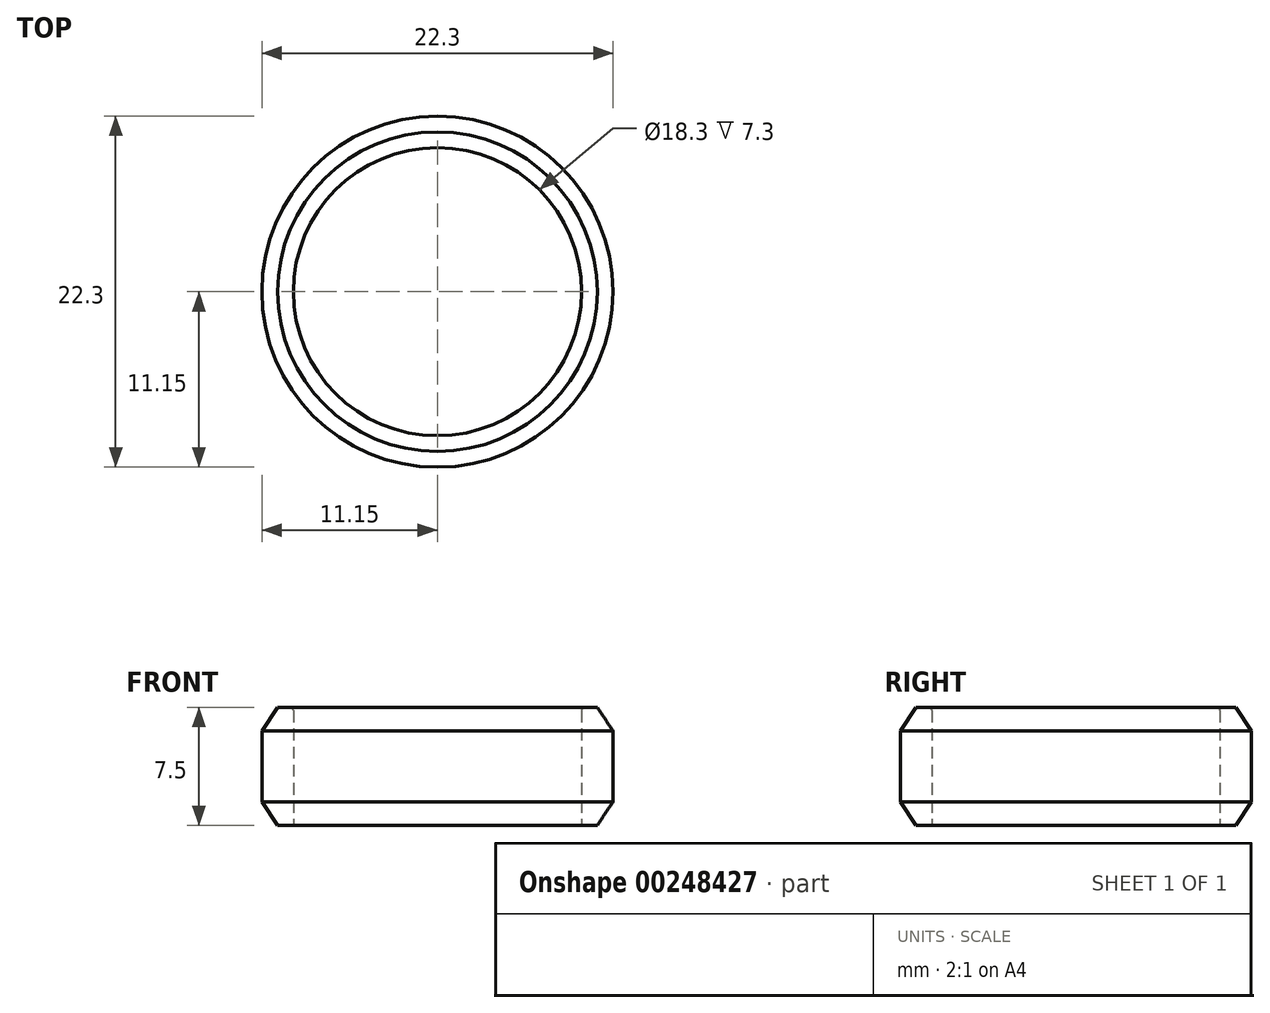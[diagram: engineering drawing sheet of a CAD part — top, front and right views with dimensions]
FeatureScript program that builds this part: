
annotation { "Feature Type Name" : "Feature", "Feature Type Description" : "" }
export const myFeature = defineFeature(function(context is Context, id is Id, definition is map)
    precondition{}
    {
        {
            var Q0;
            Q0=qCreatedBy(makeId("Top.planeOp"),FACE);
            var sketch = newSketch(context, id + "F0", { "sketchPlane" : qUnion([Q0])});
            skCircle(sketch, "E0", {"center": v(0, 0) * mm, "radius": 9.15 * mm});
            skCircle(sketch, "E1.0", {"center": v(0, 0) * mm, "radius": 11.15 * mm});
            skPoint(sketch, "E2", {"position": v(0, 10.15) * mm});
            skPoint(sketch, "E3.start.orphan", {"position": v(0, 11.15) * mm});
            skPoint(sketch, "E4.trimOffspring.end.orphan", {"position": v(0, 9.15) * mm});
            skSolve(sketch);
        }
        {
            var Q0;
            Q0=makeQuery(id+"F0.imprint","IMPRINT",FACE,{"disambiguationData":[TD([[makeQuery(id+"F0.imprint","IMPRINT",EDGE,{"derivedFrom":sQuery(id+"F0.wireOp",EDGE,"E0")}),-1.0]])]});
            var Q1;
            Q1=makeQuery(id+"F0.imprint","IMPRINT",FACE,{"disambiguationData":[TD([[makeQuery(id+"F0.imprint","IMPRINT",EDGE,{"derivedFrom":sQuery(id+"F0.wireOp",EDGE,"a28f23ed-ef4f-4aed-836b-e849da1a0182.1.61.0")}),1.0]])]});
            var Q2;
            Q2=makeQuery(id+"F0.imprint","IMPRINT",FACE,{"disambiguationData":[TD([[makeQuery(id+"F0.imprint","IMPRINT",EDGE,{"derivedFrom":sQuery(id+"F0.wireOp",EDGE,"9b5bb41e-afbc-4d25-b2b3-00661ebed94f.1.26.0")}),1.0]])]});
            var Q3;
            Q3=makeQuery(id+"F0.imprint","IMPRINT",FACE,{"disambiguationData":[TD([[makeQuery(id+"F0.imprint","IMPRINT",EDGE,{"derivedFrom":sQuery(id+"F0.wireOp",EDGE,"6a247efb-4b51-4912-8876-f2ab3c554f81.10.0")}),1.0]])]});
            var Q4;
            Q4=makeQuery(id+"F0.imprint","IMPRINT",FACE,{"disambiguationData":[TD([[makeQuery(id+"F0.imprint","IMPRINT",EDGE,{"derivedFrom":sQuery(id+"F0.wireOp",EDGE,"a28f23ed-ef4f-4aed-836b-e849da1a0182.1.75.0")}),1.0]])]});
            var Q5;
            Q5=makeQuery(id+"F0.imprint","IMPRINT",FACE,{"disambiguationData":[TD([[makeQuery(id+"F0.imprint","IMPRINT",EDGE,{"derivedFrom":sQuery(id+"F0.wireOp",EDGE,"0dfb17a8-0a4b-4796-96ea-2a2d021c0c5c.1.42.0")}),1.0]])]});
            var Q6;
            Q6=makeQuery(id+"F0.imprint","IMPRINT",FACE,{"disambiguationData":[TD([[makeQuery(id+"F0.imprint","IMPRINT",EDGE,{"derivedFrom":sQuery(id+"F0.wireOp",EDGE,"0dfb17a8-0a4b-4796-96ea-2a2d021c0c5c.1.37.0")}),1.0]])]});
            var Q7;
            Q7=makeQuery(id+"F0.imprint","IMPRINT",FACE,{"disambiguationData":[TD([[makeQuery(id+"F0.imprint","IMPRINT",EDGE,{"derivedFrom":sQuery(id+"F0.wireOp",EDGE,"6a247efb-4b51-4912-8876-f2ab3c554f81.13.0")}),1.0]])]});
            var Q8;
            Q8=makeQuery(id+"F0.imprint","IMPRINT",FACE,{"disambiguationData":[TD([[makeQuery(id+"F0.imprint","IMPRINT",EDGE,{"derivedFrom":sQuery(id+"F0.wireOp",EDGE,"a28f23ed-ef4f-4aed-836b-e849da1a0182.1.68.0")}),1.0]])]});
            var Q9;
            Q9=makeQuery(id+"F0.imprint","IMPRINT",FACE,{"disambiguationData":[TD([[makeQuery(id+"F0.imprint","IMPRINT",EDGE,{"derivedFrom":sQuery(id+"F0.wireOp",EDGE,"a28f23ed-ef4f-4aed-836b-e849da1a0182.1.71.0")}),1.0]])]});
            var Q10;
            Q10=makeQuery(id+"F0.imprint","IMPRINT",FACE,{"disambiguationData":[TD([[makeQuery(id+"F0.imprint","IMPRINT",EDGE,{"derivedFrom":sQuery(id+"F0.wireOp",EDGE,"9b5bb41e-afbc-4d25-b2b3-00661ebed94f.1.28.0")}),1.0]])]});
            var Q11;
            Q11=makeQuery(id+"F0.imprint","IMPRINT",FACE,{"disambiguationData":[TD([[makeQuery(id+"F0.imprint","IMPRINT",EDGE,{"derivedFrom":sQuery(id+"F0.wireOp",EDGE,"9b5bb41e-afbc-4d25-b2b3-00661ebed94f.1.29.0")}),1.0]])]});
            var Q12;
            Q12=makeQuery(id+"F0.imprint","IMPRINT",FACE,{"disambiguationData":[TD([[makeQuery(id+"F0.imprint","IMPRINT",EDGE,{"derivedFrom":sQuery(id+"F0.wireOp",EDGE,"0dfb17a8-0a4b-4796-96ea-2a2d021c0c5c.1.51.0")}),1.0]])]});
            var Q13;
            Q13=makeQuery(id+"F0.imprint","IMPRINT",FACE,{"disambiguationData":[TD([[makeQuery(id+"F0.imprint","IMPRINT",EDGE,{"derivedFrom":sQuery(id+"F0.wireOp",EDGE,"6a247efb-4b51-4912-8876-f2ab3c554f81.9.0")}),1.0]])]});
            var Q14;
            Q14=makeQuery(id+"F0.imprint","IMPRINT",FACE,{"disambiguationData":[TD([[makeQuery(id+"F0.imprint","IMPRINT",EDGE,{"derivedFrom":sQuery(id+"F0.wireOp",EDGE,"dd421f76-6e49-4080-92ba-426d591658a1")}),1.0]])]});
            var Q15;
            Q15=makeQuery(id+"F0.imprint","IMPRINT",FACE,{"disambiguationData":[TD([[makeQuery(id+"F0.imprint","IMPRINT",EDGE,{"derivedFrom":sQuery(id+"F0.wireOp",EDGE,"0dfb17a8-0a4b-4796-96ea-2a2d021c0c5c.1.57.0")}),1.0]])]});
            var Q16;
            Q16=makeQuery(id+"F0.imprint","IMPRINT",FACE,{"disambiguationData":[TD([[makeQuery(id+"F0.imprint","IMPRINT",EDGE,{"derivedFrom":sQuery(id+"F0.wireOp",EDGE,"a28f23ed-ef4f-4aed-836b-e849da1a0182.1.63.0")}),1.0]])]});
            var Q17;
            Q17=makeQuery(id+"F0.imprint","IMPRINT",FACE,{"disambiguationData":[TD([[makeQuery(id+"F0.imprint","IMPRINT",EDGE,{"derivedFrom":sQuery(id+"F0.wireOp",EDGE,"6a247efb-4b51-4912-8876-f2ab3c554f81.6.0")}),1.0]])]});
            var Q18;
            Q18=makeQuery(id+"F0.imprint","IMPRINT",FACE,{"disambiguationData":[TD([[makeQuery(id+"F0.imprint","IMPRINT",EDGE,{"derivedFrom":sQuery(id+"F0.wireOp",EDGE,"6a247efb-4b51-4912-8876-f2ab3c554f81.17.0")}),1.0]])]});
            var Q19;
            Q19=makeQuery(id+"F0.imprint","IMPRINT",FACE,{"disambiguationData":[TD([[makeQuery(id+"F0.imprint","IMPRINT",EDGE,{"derivedFrom":sQuery(id+"F0.wireOp",EDGE,"a28f23ed-ef4f-4aed-836b-e849da1a0182.1.74.0")}),1.0]])]});
            var Q20;
            Q20=makeQuery(id+"F0.imprint","IMPRINT",FACE,{"disambiguationData":[TD([[makeQuery(id+"F0.imprint","IMPRINT",EDGE,{"derivedFrom":sQuery(id+"F0.wireOp",EDGE,"9b5bb41e-afbc-4d25-b2b3-00661ebed94f.1.25.0")}),1.0]])]});
            var Q21;
            Q21=makeQuery(id+"F0.imprint","IMPRINT",FACE,{"disambiguationData":[TD([[makeQuery(id+"F0.imprint","IMPRINT",EDGE,{"derivedFrom":sQuery(id+"F0.wireOp",EDGE,"6a247efb-4b51-4912-8876-f2ab3c554f81.22.0")}),1.0]])]});
            var Q22;
            Q22=makeQuery(id+"F0.imprint","IMPRINT",FACE,{"disambiguationData":[TD([[makeQuery(id+"F0.imprint","IMPRINT",EDGE,{"derivedFrom":sQuery(id+"F0.wireOp",EDGE,"6a247efb-4b51-4912-8876-f2ab3c554f81.14.0")}),1.0]])]});
            var Q23;
            Q23=makeQuery(id+"F0.imprint","IMPRINT",FACE,{"disambiguationData":[TD([[makeQuery(id+"F0.imprint","IMPRINT",EDGE,{"derivedFrom":sQuery(id+"F0.wireOp",EDGE,"a28f23ed-ef4f-4aed-836b-e849da1a0182.1.77.0")}),1.0]])]});
            var Q24;
            Q24=makeQuery(id+"F0.imprint","IMPRINT",FACE,{"disambiguationData":[TD([[makeQuery(id+"F0.imprint","IMPRINT",EDGE,{"derivedFrom":sQuery(id+"F0.wireOp",EDGE,"6a247efb-4b51-4912-8876-f2ab3c554f81.16.0")}),1.0]])]});
            var Q25;
            Q25=makeQuery(id+"F0.imprint","IMPRINT",FACE,{"disambiguationData":[TD([[makeQuery(id+"F0.imprint","IMPRINT",EDGE,{"derivedFrom":sQuery(id+"F0.wireOp",EDGE,"a28f23ed-ef4f-4aed-836b-e849da1a0182.1.64.0")}),1.0]])]});
            var Q26;
            Q26=makeQuery(id+"F0.imprint","IMPRINT",FACE,{"disambiguationData":[TD([[makeQuery(id+"F0.imprint","IMPRINT",EDGE,{"derivedFrom":sQuery(id+"F0.wireOp",EDGE,"9b5bb41e-afbc-4d25-b2b3-00661ebed94f.1.31.0")}),1.0]])]});
            var Q27;
            Q27=makeQuery(id+"F0.imprint","IMPRINT",FACE,{"disambiguationData":[TD([[makeQuery(id+"F0.imprint","IMPRINT",EDGE,{"derivedFrom":sQuery(id+"F0.wireOp",EDGE,"6a247efb-4b51-4912-8876-f2ab3c554f81.2.0")}),1.0]])]});
            var Q28;
            Q28=makeQuery(id+"F0.imprint","IMPRINT",FACE,{"disambiguationData":[TD([[makeQuery(id+"F0.imprint","IMPRINT",EDGE,{"derivedFrom":sQuery(id+"F0.wireOp",EDGE,"6a247efb-4b51-4912-8876-f2ab3c554f81.20.0")}),1.0]])]});
            var Q29;
            Q29=makeQuery(id+"F0.imprint","IMPRINT",FACE,{"disambiguationData":[TD([[makeQuery(id+"F0.imprint","IMPRINT",EDGE,{"derivedFrom":sQuery(id+"F0.wireOp",EDGE,"a28f23ed-ef4f-4aed-836b-e849da1a0182.1.69.0")}),1.0]])]});
            var Q30;
            Q30=makeQuery(id+"F0.imprint","IMPRINT",FACE,{"disambiguationData":[TD([[makeQuery(id+"F0.imprint","IMPRINT",EDGE,{"derivedFrom":sQuery(id+"F0.wireOp",EDGE,"0dfb17a8-0a4b-4796-96ea-2a2d021c0c5c.1.59.0")}),1.0]])]});
            var Q31;
            Q31=makeQuery(id+"F0.imprint","IMPRINT",FACE,{"disambiguationData":[TD([[makeQuery(id+"F0.imprint","IMPRINT",EDGE,{"derivedFrom":sQuery(id+"F0.wireOp",EDGE,"6a247efb-4b51-4912-8876-f2ab3c554f81.15.0")}),1.0]])]});
            var Q32;
            Q32=makeQuery(id+"F0.imprint","IMPRINT",FACE,{"disambiguationData":[TD([[makeQuery(id+"F0.imprint","IMPRINT",EDGE,{"derivedFrom":sQuery(id+"F0.wireOp",EDGE,"6a247efb-4b51-4912-8876-f2ab3c554f81.4.0")}),1.0]])]});
            var Q33;
            Q33=makeQuery(id+"F0.imprint","IMPRINT",FACE,{"disambiguationData":[TD([[makeQuery(id+"F0.imprint","IMPRINT",EDGE,{"derivedFrom":sQuery(id+"F0.wireOp",EDGE,"0dfb17a8-0a4b-4796-96ea-2a2d021c0c5c.1.55.0")}),1.0]])]});
            var Q34;
            Q34=makeQuery(id+"F0.imprint","IMPRINT",FACE,{"disambiguationData":[TD([[makeQuery(id+"F0.imprint","IMPRINT",EDGE,{"derivedFrom":sQuery(id+"F0.wireOp",EDGE,"a28f23ed-ef4f-4aed-836b-e849da1a0182.1.62.0")}),1.0]])]});
            var Q35;
            Q35=makeQuery(id+"F0.imprint","IMPRINT",FACE,{"disambiguationData":[TD([[makeQuery(id+"F0.imprint","IMPRINT",EDGE,{"derivedFrom":sQuery(id+"F0.wireOp",EDGE,"0dfb17a8-0a4b-4796-96ea-2a2d021c0c5c.1.39.0")}),1.0]])]});
            var Q36;
            Q36=makeQuery(id+"F0.imprint","IMPRINT",FACE,{"disambiguationData":[TD([[makeQuery(id+"F0.imprint","IMPRINT",EDGE,{"derivedFrom":sQuery(id+"F0.wireOp",EDGE,"6a247efb-4b51-4912-8876-f2ab3c554f81.7.0")}),1.0]])]});
            var Q37;
            Q37=makeQuery(id+"F0.imprint","IMPRINT",FACE,{"disambiguationData":[TD([[makeQuery(id+"F0.imprint","IMPRINT",EDGE,{"derivedFrom":sQuery(id+"F0.wireOp",EDGE,"0dfb17a8-0a4b-4796-96ea-2a2d021c0c5c.1.45.0")}),1.0]])]});
            var Q38;
            Q38=makeQuery(id+"F0.imprint","IMPRINT",FACE,{"disambiguationData":[TD([[makeQuery(id+"F0.imprint","IMPRINT",EDGE,{"derivedFrom":sQuery(id+"F0.wireOp",EDGE,"6a247efb-4b51-4912-8876-f2ab3c554f81.11.0")}),1.0]])]});
            var Q39;
            Q39=makeQuery(id+"F0.imprint","IMPRINT",FACE,{"disambiguationData":[TD([[makeQuery(id+"F0.imprint","IMPRINT",EDGE,{"derivedFrom":sQuery(id+"F0.wireOp",EDGE,"0dfb17a8-0a4b-4796-96ea-2a2d021c0c5c.1.43.0")}),1.0]])]});
            var Q40;
            Q40=makeQuery(id+"F0.imprint","IMPRINT",FACE,{"disambiguationData":[TD([[makeQuery(id+"F0.imprint","IMPRINT",EDGE,{"derivedFrom":sQuery(id+"F0.wireOp",EDGE,"0dfb17a8-0a4b-4796-96ea-2a2d021c0c5c.1.54.0")}),1.0]])]});
            var Q41;
            Q41=makeQuery(id+"F0.imprint","IMPRINT",FACE,{"disambiguationData":[TD([[makeQuery(id+"F0.imprint","IMPRINT",EDGE,{"derivedFrom":sQuery(id+"F0.wireOp",EDGE,"6a247efb-4b51-4912-8876-f2ab3c554f81.1.0")}),1.0]])]});
            var Q42;
            Q42=makeQuery(id+"F0.imprint","IMPRINT",FACE,{"disambiguationData":[TD([[makeQuery(id+"F0.imprint","IMPRINT",EDGE,{"derivedFrom":sQuery(id+"F0.wireOp",EDGE,"a28f23ed-ef4f-4aed-836b-e849da1a0182.1.70.0")}),1.0]])]});
            var Q43;
            Q43=makeQuery(id+"F0.imprint","IMPRINT",FACE,{"disambiguationData":[TD([[makeQuery(id+"F0.imprint","IMPRINT",EDGE,{"derivedFrom":sQuery(id+"F0.wireOp",EDGE,"0dfb17a8-0a4b-4796-96ea-2a2d021c0c5c.1.38.0")}),1.0]])]});
            var Q44;
            Q44=makeQuery(id+"F0.imprint","IMPRINT",FACE,{"disambiguationData":[TD([[makeQuery(id+"F0.imprint","IMPRINT",EDGE,{"derivedFrom":sQuery(id+"F0.wireOp",EDGE,"0dfb17a8-0a4b-4796-96ea-2a2d021c0c5c.1.48.0")}),1.0]])]});
            var Q45;
            Q45=makeQuery(id+"F0.imprint","IMPRINT",FACE,{"disambiguationData":[TD([[makeQuery(id+"F0.imprint","IMPRINT",EDGE,{"derivedFrom":sQuery(id+"F0.wireOp",EDGE,"a28f23ed-ef4f-4aed-836b-e849da1a0182.1.76.0")}),1.0]])]});
            var Q46;
            Q46=makeQuery(id+"F0.imprint","IMPRINT",FACE,{"disambiguationData":[TD([[makeQuery(id+"F0.imprint","IMPRINT",EDGE,{"derivedFrom":sQuery(id+"F0.wireOp",EDGE,"0dfb17a8-0a4b-4796-96ea-2a2d021c0c5c.1.50.0")}),1.0]])]});
            var Q47;
            Q47=makeQuery(id+"F0.imprint","IMPRINT",FACE,{"disambiguationData":[TD([[makeQuery(id+"F0.imprint","IMPRINT",EDGE,{"derivedFrom":sQuery(id+"F0.wireOp",EDGE,"6a247efb-4b51-4912-8876-f2ab3c554f81.18.0")}),1.0]])]});
            var Q48;
            Q48=makeQuery(id+"F0.imprint","IMPRINT",FACE,{"disambiguationData":[TD([[makeQuery(id+"F0.imprint","IMPRINT",EDGE,{"derivedFrom":sQuery(id+"F0.wireOp",EDGE,"9b5bb41e-afbc-4d25-b2b3-00661ebed94f.1.33.0")}),1.0]])]});
            var Q49;
            Q49=makeQuery(id+"F0.imprint","IMPRINT",FACE,{"disambiguationData":[TD([[makeQuery(id+"F0.imprint","IMPRINT",EDGE,{"derivedFrom":sQuery(id+"F0.wireOp",EDGE,"a28f23ed-ef4f-4aed-836b-e849da1a0182.1.65.0")}),1.0]])]});
            var Q50;
            Q50=makeQuery(id+"F0.imprint","IMPRINT",FACE,{"disambiguationData":[TD([[makeQuery(id+"F0.imprint","IMPRINT",EDGE,{"derivedFrom":sQuery(id+"F0.wireOp",EDGE,"0dfb17a8-0a4b-4796-96ea-2a2d021c0c5c.1.49.0")}),1.0]])]});
            var Q51;
            Q51=makeQuery(id+"F0.imprint","IMPRINT",FACE,{"disambiguationData":[TD([[makeQuery(id+"F0.imprint","IMPRINT",EDGE,{"derivedFrom":sQuery(id+"F0.wireOp",EDGE,"6a247efb-4b51-4912-8876-f2ab3c554f81.23.0")}),1.0]])]});
            var Q52;
            Q52=makeQuery(id+"F0.imprint","IMPRINT",FACE,{"disambiguationData":[TD([[makeQuery(id+"F0.imprint","IMPRINT",EDGE,{"derivedFrom":sQuery(id+"F0.wireOp",EDGE,"0dfb17a8-0a4b-4796-96ea-2a2d021c0c5c.1.58.0")}),1.0]])]});
            var Q53;
            Q53=makeQuery(id+"F0.imprint","IMPRINT",FACE,{"disambiguationData":[TD([[makeQuery(id+"F0.imprint","IMPRINT",EDGE,{"derivedFrom":sQuery(id+"F0.wireOp",EDGE,"6a247efb-4b51-4912-8876-f2ab3c554f81.12.0")}),1.0]])]});
            var Q54;
            Q54=makeQuery(id+"F0.imprint","IMPRINT",FACE,{"disambiguationData":[TD([[makeQuery(id+"F0.imprint","IMPRINT",EDGE,{"derivedFrom":sQuery(id+"F0.wireOp",EDGE,"9b5bb41e-afbc-4d25-b2b3-00661ebed94f.1.32.0")}),1.0]])]});
            var Q55;
            Q55=makeQuery(id+"F0.imprint","IMPRINT",FACE,{"disambiguationData":[TD([[makeQuery(id+"F0.imprint","IMPRINT",EDGE,{"derivedFrom":sQuery(id+"F0.wireOp",EDGE,"0dfb17a8-0a4b-4796-96ea-2a2d021c0c5c.1.41.0")}),1.0]])]});
            var Q56;
            Q56=makeQuery(id+"F0.imprint","IMPRINT",FACE,{"disambiguationData":[TD([[makeQuery(id+"F0.imprint","IMPRINT",EDGE,{"derivedFrom":sQuery(id+"F0.wireOp",EDGE,"9b5bb41e-afbc-4d25-b2b3-00661ebed94f.1.34.0")}),1.0]])]});
            var Q57;
            Q57=makeQuery(id+"F0.imprint","IMPRINT",FACE,{"disambiguationData":[TD([[makeQuery(id+"F0.imprint","IMPRINT",EDGE,{"derivedFrom":sQuery(id+"F0.wireOp",EDGE,"a28f23ed-ef4f-4aed-836b-e849da1a0182.1.67.0")}),1.0]])]});
            var Q58;
            Q58=makeQuery(id+"F0.imprint","IMPRINT",FACE,{"disambiguationData":[TD([[makeQuery(id+"F0.imprint","IMPRINT",EDGE,{"derivedFrom":sQuery(id+"F0.wireOp",EDGE,"0dfb17a8-0a4b-4796-96ea-2a2d021c0c5c.1.46.0")}),1.0]])]});
            var Q59;
            Q59=makeQuery(id+"F0.imprint","IMPRINT",FACE,{"disambiguationData":[TD([[makeQuery(id+"F0.imprint","IMPRINT",EDGE,{"derivedFrom":sQuery(id+"F0.wireOp",EDGE,"0dfb17a8-0a4b-4796-96ea-2a2d021c0c5c.1.36.0")}),1.0]])]});
            var Q60;
            Q60=makeQuery(id+"F0.imprint","IMPRINT",FACE,{"disambiguationData":[TD([[makeQuery(id+"F0.imprint","IMPRINT",EDGE,{"derivedFrom":sQuery(id+"F0.wireOp",EDGE,"a28f23ed-ef4f-4aed-836b-e849da1a0182.1.60.0")}),1.0]])]});
            var Q61;
            Q61=makeQuery(id+"F0.imprint","IMPRINT",FACE,{"disambiguationData":[TD([[makeQuery(id+"F0.imprint","IMPRINT",EDGE,{"derivedFrom":sQuery(id+"F0.wireOp",EDGE,"a28f23ed-ef4f-4aed-836b-e849da1a0182.1.66.0")}),1.0]])]});
            var Q62;
            Q62=makeQuery(id+"F0.imprint","IMPRINT",FACE,{"disambiguationData":[TD([[makeQuery(id+"F0.imprint","IMPRINT",EDGE,{"derivedFrom":sQuery(id+"F0.wireOp",EDGE,"0dfb17a8-0a4b-4796-96ea-2a2d021c0c5c.1.56.0")}),1.0]])]});
            var Q63;
            Q63=makeQuery(id+"F0.imprint","IMPRINT",FACE,{"disambiguationData":[TD([[makeQuery(id+"F0.imprint","IMPRINT",EDGE,{"derivedFrom":sQuery(id+"F0.wireOp",EDGE,"9b5bb41e-afbc-4d25-b2b3-00661ebed94f.1.30.0")}),1.0]])]});
            var Q64;
            Q64=makeQuery(id+"F0.imprint","IMPRINT",FACE,{"disambiguationData":[TD([[makeQuery(id+"F0.imprint","IMPRINT",EDGE,{"derivedFrom":sQuery(id+"F0.wireOp",EDGE,"6a247efb-4b51-4912-8876-f2ab3c554f81.8.0")}),1.0]])]});
            var Q65;
            Q65=makeQuery(id+"F0.imprint","IMPRINT",FACE,{"disambiguationData":[TD([[makeQuery(id+"F0.imprint","IMPRINT",EDGE,{"derivedFrom":sQuery(id+"F0.wireOp",EDGE,"0dfb17a8-0a4b-4796-96ea-2a2d021c0c5c.1.52.0")}),1.0]])]});
            var Q66;
            Q66=makeQuery(id+"F0.imprint","IMPRINT",FACE,{"disambiguationData":[TD([[makeQuery(id+"F0.imprint","IMPRINT",EDGE,{"derivedFrom":sQuery(id+"F0.wireOp",EDGE,"0dfb17a8-0a4b-4796-96ea-2a2d021c0c5c.1.53.0")}),1.0]])]});
            var Q67;
            Q67=makeQuery(id+"F0.imprint","IMPRINT",FACE,{"disambiguationData":[TD([[makeQuery(id+"F0.imprint","IMPRINT",EDGE,{"derivedFrom":sQuery(id+"F0.wireOp",EDGE,"6a247efb-4b51-4912-8876-f2ab3c554f81.5.0")}),1.0]])]});
            var Q68;
            Q68=makeQuery(id+"F0.imprint","IMPRINT",FACE,{"disambiguationData":[TD([[makeQuery(id+"F0.imprint","IMPRINT",EDGE,{"derivedFrom":sQuery(id+"F0.wireOp",EDGE,"a28f23ed-ef4f-4aed-836b-e849da1a0182.1.72.0")}),1.0]])]});
            var Q69;
            Q69=makeQuery(id+"F0.imprint","IMPRINT",FACE,{"disambiguationData":[TD([[makeQuery(id+"F0.imprint","IMPRINT",EDGE,{"derivedFrom":sQuery(id+"F0.wireOp",EDGE,"0dfb17a8-0a4b-4796-96ea-2a2d021c0c5c.1.40.0")}),1.0]])]});
            var Q70;
            Q70=makeQuery(id+"F0.imprint","IMPRINT",FACE,{"disambiguationData":[TD([[makeQuery(id+"F0.imprint","IMPRINT",EDGE,{"derivedFrom":sQuery(id+"F0.wireOp",EDGE,"0dfb17a8-0a4b-4796-96ea-2a2d021c0c5c.1.47.0")}),1.0]])]});
            var Q71;
            Q71=makeQuery(id+"F0.imprint","IMPRINT",FACE,{"disambiguationData":[TD([[makeQuery(id+"F0.imprint","IMPRINT",EDGE,{"derivedFrom":sQuery(id+"F0.wireOp",EDGE,"6a247efb-4b51-4912-8876-f2ab3c554f81.3.0")}),1.0]])]});
            var Q72;
            Q72=makeQuery(id+"F0.imprint","IMPRINT",FACE,{"disambiguationData":[TD([[makeQuery(id+"F0.imprint","IMPRINT",EDGE,{"derivedFrom":sQuery(id+"F0.wireOp",EDGE,"a28f23ed-ef4f-4aed-836b-e849da1a0182.1.79.0")}),1.0]])]});
            var Q73;
            Q73=makeQuery(id+"F0.imprint","IMPRINT",FACE,{"disambiguationData":[TD([[makeQuery(id+"F0.imprint","IMPRINT",EDGE,{"derivedFrom":sQuery(id+"F0.wireOp",EDGE,"6a247efb-4b51-4912-8876-f2ab3c554f81.24.0")}),1.0]])]});
            var Q74;
            Q74=makeQuery(id+"F0.imprint","IMPRINT",FACE,{"disambiguationData":[TD([[makeQuery(id+"F0.imprint","IMPRINT",EDGE,{"derivedFrom":sQuery(id+"F0.wireOp",EDGE,"a28f23ed-ef4f-4aed-836b-e849da1a0182.1.78.0")}),1.0]])]});
            var Q75;
            Q75=makeQuery(id+"F0.imprint","IMPRINT",FACE,{"disambiguationData":[TD([[makeQuery(id+"F0.imprint","IMPRINT",EDGE,{"derivedFrom":sQuery(id+"F0.wireOp",EDGE,"6a247efb-4b51-4912-8876-f2ab3c554f81.21.0")}),1.0]])]});
            var Q76;
            Q76=makeQuery(id+"F0.imprint","IMPRINT",FACE,{"disambiguationData":[TD([[makeQuery(id+"F0.imprint","IMPRINT",EDGE,{"derivedFrom":sQuery(id+"F0.wireOp",EDGE,"0dfb17a8-0a4b-4796-96ea-2a2d021c0c5c.1.44.0")}),1.0]])]});
            var Q77;
            Q77=makeQuery(id+"F0.imprint","IMPRINT",FACE,{"disambiguationData":[TD([[makeQuery(id+"F0.imprint","IMPRINT",EDGE,{"derivedFrom":sQuery(id+"F0.wireOp",EDGE,"9b5bb41e-afbc-4d25-b2b3-00661ebed94f.1.27.0")}),1.0]])]});
            var Q78;
            Q78=makeQuery(id+"F0.imprint","IMPRINT",FACE,{"disambiguationData":[TD([[makeQuery(id+"F0.imprint","IMPRINT",EDGE,{"derivedFrom":sQuery(id+"F0.wireOp",EDGE,"a28f23ed-ef4f-4aed-836b-e849da1a0182.1.73.0")}),1.0]])]});
            var Q79;
            Q79=makeQuery(id+"F0.imprint","IMPRINT",FACE,{"disambiguationData":[TD([[makeQuery(id+"F0.imprint","IMPRINT",EDGE,{"derivedFrom":sQuery(id+"F0.wireOp",EDGE,"0dfb17a8-0a4b-4796-96ea-2a2d021c0c5c.1.35.0")}),1.0]])]});
            var Q80;
            Q80=makeQuery(id+"F0.imprint","IMPRINT",FACE,{"disambiguationData":[TD([[makeQuery(id+"F0.imprint","IMPRINT",EDGE,{"derivedFrom":sQuery(id+"F0.wireOp",EDGE,"6a247efb-4b51-4912-8876-f2ab3c554f81.19.0")}),1.0]])]});
            extrude(context, id + "F1", {"entities" : qUnion([Q0, Q1, Q2, Q3, Q4, Q5, Q6, Q7, Q8, Q9, Q10, Q11, Q12, Q13, Q14, Q15, Q16, Q17, Q18, Q19, Q20, Q21, Q22, Q23, Q24, Q25, Q26, Q27, Q28, Q29, Q30, Q31, Q32, Q33, Q34, Q35, Q36, Q37, Q38, Q39, Q40, Q41, Q42, Q43, Q44, Q45, Q46, Q47, Q48, Q49, Q50, Q51, Q52, Q53, Q54, Q55, Q56, Q57, Q58, Q59, Q60, Q61, Q62, Q63, Q64, Q65, Q66, Q67, Q68, Q69, Q70, Q71, Q72, Q73, Q74, Q75, Q76, Q77, Q78, Q79, Q80]), "depth" : 7.5 * mm});
        }
        {
            var Q0;
            Q0=makeQuery(id+"F1.opExtrude","CAP_EDGE",EDGE,{"disambiguationData":[OSD([sQuery(id+"F0.wireOp",EDGE,"E1.0")])],"isStart":false});
            var Q1;
            Q1=makeQuery(id+"F1.opExtrude","CAP_EDGE",EDGE,{"disambiguationData":[OSD([sQuery(id+"F0.wireOp",EDGE,"E1.0")])],"isStart":true});
            chamfer(context, id + "F2", {"entities" : qUnion([Q0, Q1]), "chamferType" : ChamferType.TWO_OFFSETS, "width1" : 1 * mm, "oppositeDirection" : false, "width2" : 1.5 * mm, "tangentPropagation" : true});
        }
        {
            var Q0;
            Q0=makeQuery(id+"F1.opExtrude","CAP_EDGE",EDGE,{"disambiguationData":[OSD([sQuery(id+"F0.wireOp",EDGE,"E0")])],"isStart":false});
            fillet(context, id + "F3", {"entities" : qUnion([Q0]), "radius" : .2 * mm, "tangentPropagation" : true, "allowEdgeOverflow" : false});
        }
    });
